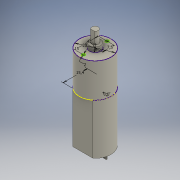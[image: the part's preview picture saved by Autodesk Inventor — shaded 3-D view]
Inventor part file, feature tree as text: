
AUTODESK INVENTOR PART (.ipt)
format: ipt  version: 2020 (Build 240168000, 168)  size: 174,080 bytes
history: native  units: mm
features: extrude x7, sketch x5, hole x2, other x1
ambient origin geometry x8: Origin, YZ Plane, XZ Plane, XY Plane, X Axis, Y Axis, Z Axis, Center Point
bodies: Body1 (feature_tree)
feature tree (15):
  other  "Твердое тело1"
  sketch  "Эскиз1"
  extrude  "Выдавливание1"  Depth=20.0mm
  extrude  "Выдавливание2"  Depth=7.0mm
  extrude  "Выдавливание3"  Depth=4.0mm
  extrude  "Выдавливание4"  Depth=21.6mm TaperAngle=0.0deg
  sketch  "Эскиз3"
  extrude  "Выдавливание5"  Depth=3.0mm TaperAngle=0.0deg
  extrude  "Выдавливание6"  Depth=10.5mm TaperAngle=0.0deg
  extrude  "Выдавливание7"  Depth=1.5mm
  sketch  "Эскиз5"
  hole  "Отверстие1"  [1 undecoded]
  hole  "Отверстие2"  [1 undecoded]
  sketch  "Эскиз2"
  sketch  "Эскиз4"
note: 2 required parameter values undecoded (feature->parameter linkage not recoverable at this tier; creation-order binding heuristic only, values carry confidence <= 0.55)
